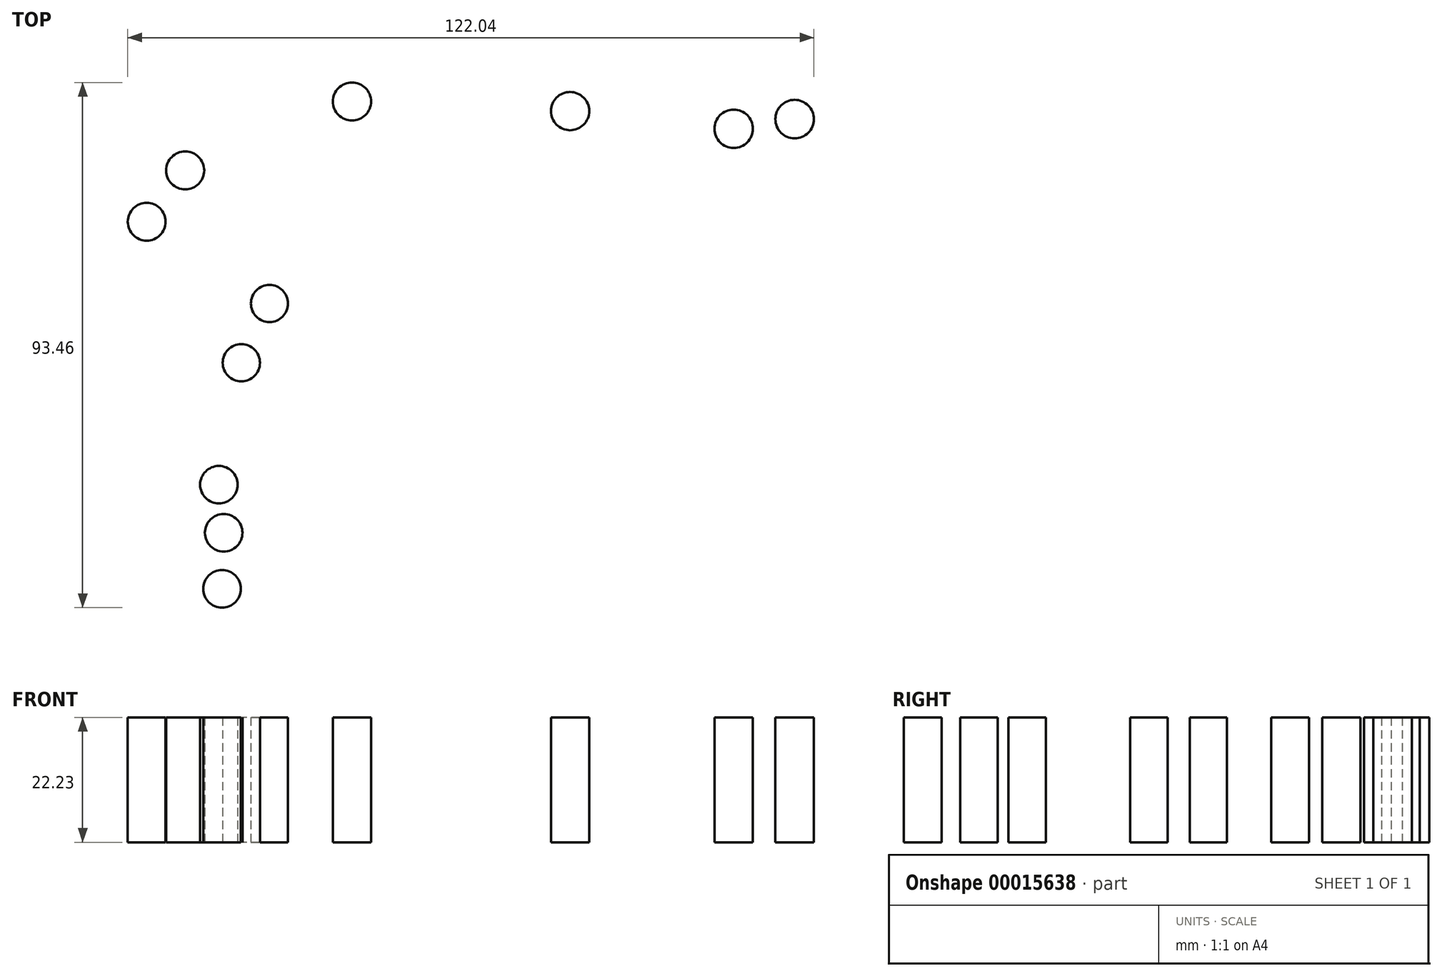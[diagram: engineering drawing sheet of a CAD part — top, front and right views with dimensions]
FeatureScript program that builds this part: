
annotation { "Feature Type Name" : "Feature", "Feature Type Description" : "" }
export const myFeature = defineFeature(function(context is Context, id is Id, definition is map)
    precondition{}
    {
        {
            var Q0;
            Q0=qCreatedBy(makeId("Top.planeOp"),FACE);
            var sketch = newSketch(context, id + "F0", { "sketchPlane" : qUnion([Q0])});
            skCircle(sketch, "E0", {"center": v(-42.91, 14.12) * mm, "radius": 3.3 * mm});
            skCircle(sketch, "E1", {"center": v(-47.92, 3.57) * mm, "radius": 3.31 * mm});
            skCircle(sketch, "E2", {"center": v(-51.91, -18.11) * mm, "radius": 3.33 * mm});
            skCircle(sketch, "E3", {"center": v(-51.06, -26.67) * mm, "radius": 3.34 * mm});
            skCircle(sketch, "E4", {"center": v(-51.34, -36.65) * mm, "radius": 3.35 * mm});
            skCircle(sketch, "E5", {"center": v(-57.9, 37.8) * mm, "radius": 3.38 * mm});
            skCircle(sketch, "E6", {"center": v(-64.75, 28.67) * mm, "radius": 3.37 * mm});
            skCircle(sketch, "E7", {"center": v(-28.24, 50.06) * mm, "radius": 3.4 * mm});
            skCircle(sketch, "E8", {"center": v(10.55, 48.35) * mm, "radius": 3.4 * mm});
            skCircle(sketch, "E9", {"center": v(39.65, 45.21) * mm, "radius": 3.42 * mm});
            skCircle(sketch, "E10", {"center": v(50.49, 46.92) * mm, "radius": 3.43 * mm});
            skSolve(sketch);
        }
        {
            var Q0;
            Q0 = qSketchRegion(id + "F0", true);
            extrude(context, id + "F1", {"entities" : qUnion([Q0]), "depth" : 22.22 * mm});
        }
    });
